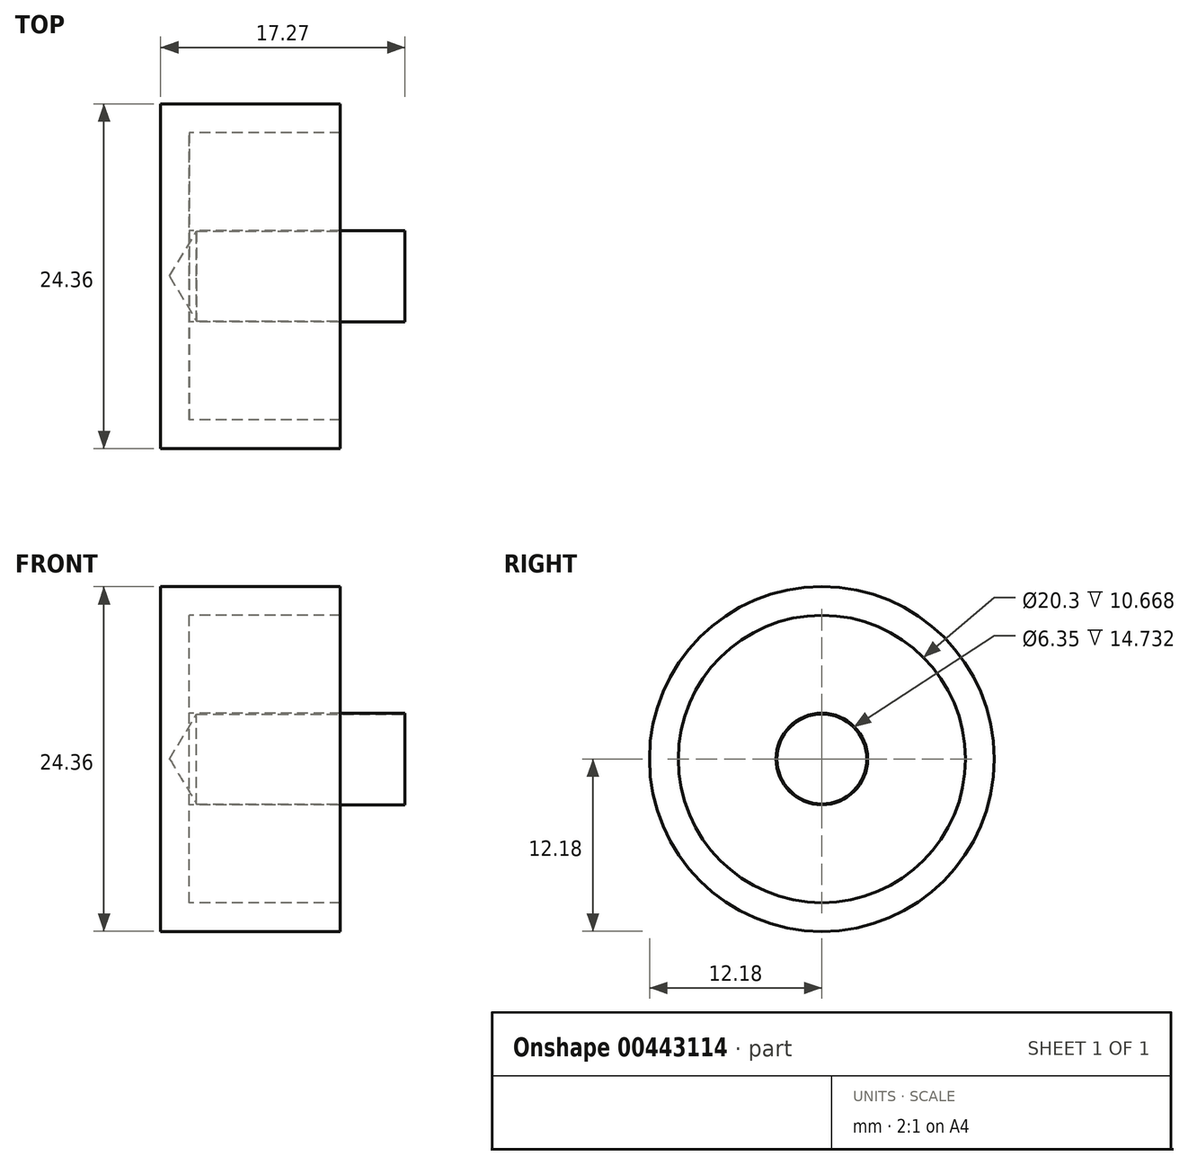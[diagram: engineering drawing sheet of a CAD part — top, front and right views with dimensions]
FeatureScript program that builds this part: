
annotation { "Feature Type Name" : "Feature", "Feature Type Description" : "" }
export const myFeature = defineFeature(function(context is Context, id is Id, definition is map)
    precondition{}
    {
        {
            var Q0;
            Q0=qCreatedBy(makeId("Right.planeOp"),FACE);
            var sketch = newSketch(context, id + "F0", { "sketchPlane" : qUnion([Q0])});
            skCircle(sketch, "E0", {"center": v(0, 0) * mm, "radius": 12.18 * mm});
            skSolve(sketch);
        }
        {
            var Q0;
            Q0=makeQuery(id+"F0.imprint","IMPRINT",FACE,{"disambiguationData":[TD([[makeQuery(id+"F0.imprint","IMPRINT",EDGE,{"derivedFrom":sQuery(id+"F0.wireOp",EDGE,"E0")}),1.0]])]});
            extrude(context, id + "F1", {"entities" : qUnion([Q0]), "depth" : 12.7 * mm});
        }
        {
            var Q0;
            Q0=makeQuery(id+"F1.opExtrude","CAP_FACE",FACE,{"disambiguationData":[OSD([sQuery(id+"F0.wireOp",EDGE,"E0")])],"isStart":false});
            shell(context, id + "F2", {"entities" : qUnion([Q0]), "thickness" : 2.03 * mm});
        }
        {
            var Q0;
            {var subQ0=sQuery(id+"F0.wireOp",EDGE,"E0");Q0=makeQuery(id+"F2.opShell","OFFSET_FACE",FACE,{"disambiguationData":[OSD([subQ0]),TDD([makeQuery(id+"F1.opExtrude","CAP_FACE",FACE,{"disambiguationData":[OSD([subQ0])],"isStart":true})])]});}
            var sketch = newSketch(context, id + "F3", { "sketchPlane" : qUnion([Q0])});
            skCircle(sketch, "E1", {"center": v(0, 0) * mm, "radius": 3.24 * mm});
            skSolve(sketch);
        }
        {
            var Q0;
            Q0 = qSketchRegion(id + "F3", true);
            extrude(context, id + "F4", {"entities" : qUnion([Q0]), "operationType" : NewBodyOperationType.ADD, "depth" : 15.24 * mm});
        }
        {
            var Q0;
            Q0=makeQuery(id+"F4.opExtrude","CAP_FACE",FACE,{"disambiguationData":[OSD([sQuery(id+"F3.wireOp",EDGE,"E1")])],"isStart":false});
            var sketch = newSketch(context, id + "F5", { "sketchPlane" : qUnion([Q0])});
            skPoint(sketch, "E2", {"position": v(0, 0) * mm});
            skSolve(sketch);
        }
        {
            var Q0;
            Q0=sQuery(id+"F5.wireOp",VERTEX,"E2");
            var Q1;
            Q1=makeQuery(id+"F1.opExtrude","SWEPT_BODY",BODY,{"disambiguationData":[OSD([sQuery(id+"F0.wireOp",EDGE,"E0")])]});
            hole(context, id + "F6", {"style" : HoleStyle.SIMPLE, "endStyle" : HoleEndStyle.BLIND, "holeDiameter" : 6.35 * mm, "holeDepth" : 14.73 * mm, "isTappedThrough" : true, "tappedDepth" : 12.7 * mm, "tapClearance" : 3, "locations" : qUnion([Q0]), "scope" : qUnion([Q1])});
        }
    });
